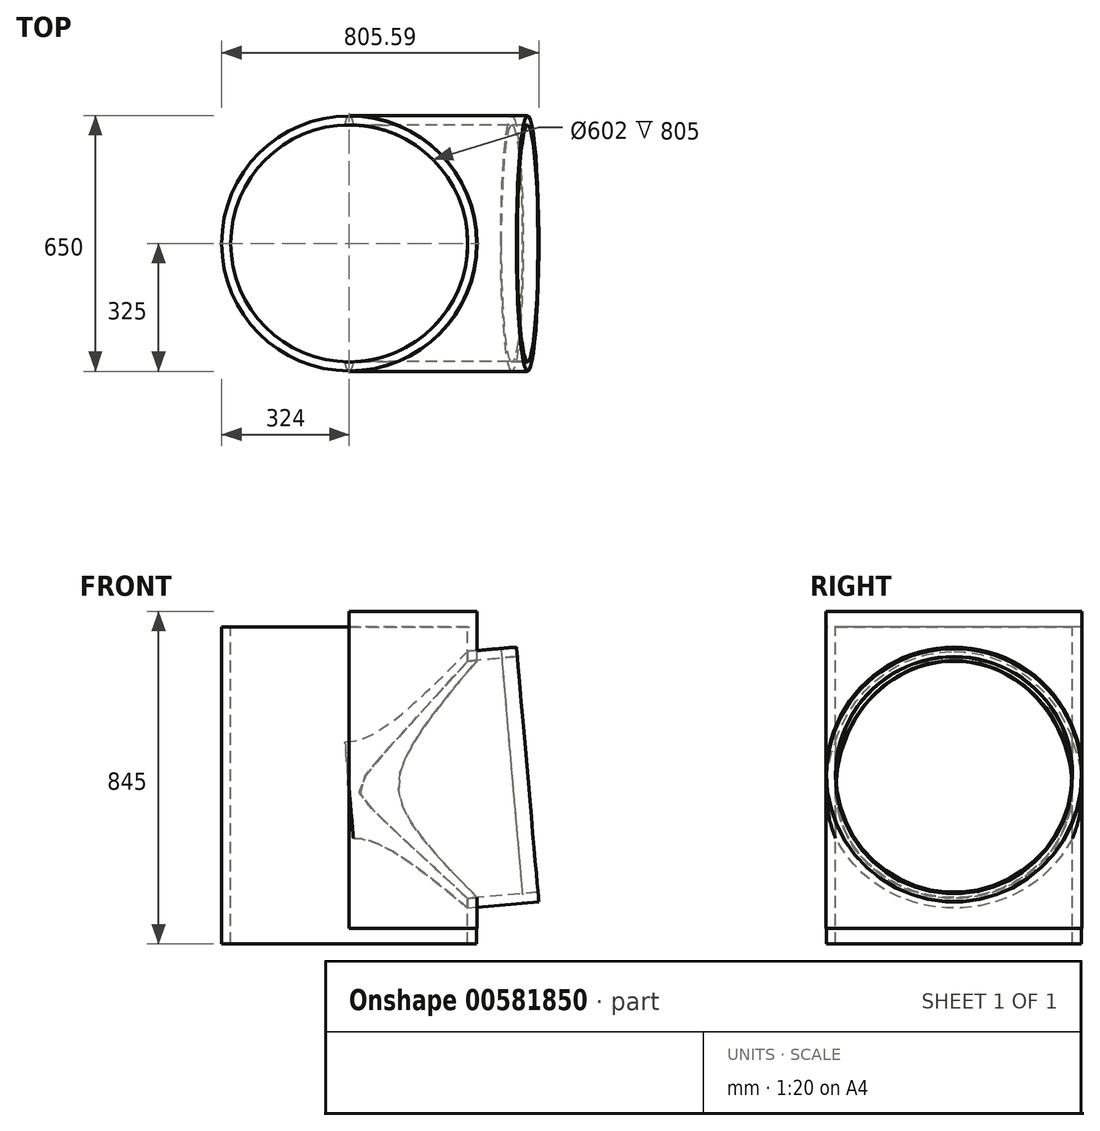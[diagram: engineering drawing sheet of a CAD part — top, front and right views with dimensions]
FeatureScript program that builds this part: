
annotation { "Feature Type Name" : "Feature", "Feature Type Description" : "" }
export const myFeature = defineFeature(function(context is Context, id is Id, definition is map)
    precondition{}
    {
        {
            var Q0;
            Q0=qCreatedBy(makeId("Front.planeOp"),FACE);
            var sketch = newSketch(context, id + "F0", { "sketchPlane" : qUnion([Q0])});
            skLineSegment(sketch, "E0", {"start": v(0, 377.94) * mm, "end": v(0, -525.84) * mm, "construction": true});
            skLineSegment(sketch, "E1", {"start": v(-325, -351) * mm, "end": v(-324, -351) * mm});
            skLineSegment(sketch, "E2", {"start": v(-324, -391) * mm, "end": v(-324, -351) * mm});
            skLineSegment(sketch, "E3", {"start": v(-324, -391) * mm, "end": v(-301, -391) * mm});
            skLineSegment(sketch, "E4", {"start": v(-301, -351) * mm, "end": v(-301, -391) * mm});
            skLineSegment(sketch, "E5", {"start": v(-301, -351) * mm, "end": v(-300, -351) * mm});
            skLineSegment(sketch, "E6", {"start": v(-576.36, 528.14) * mm, "end": v(633, -580.04) * mm, "construction": true});
            skLineSegment(sketch, "E7", {"start": v(0, 0) * mm, "end": v(-755.87, 0) * mm, "construction": true});
            skLineSegment(sketch, "E8", {"start": v(0, 0) * mm, "end": v(-73.8, 843.63) * mm, "construction": true});
            skLineSegment(sketch, "E9", {"start": v(-325, -351) * mm, "end": v(-325, 297.8) * mm});
            skLineSegment(sketch, "E10", {"start": v(-300, -351) * mm, "end": v(-300, 274.9) * mm});
            skLineSegment(sketch, "E11", {"start": v(424.94, 363.42) * mm, "end": v(425.03, 362.42) * mm});
            skLineSegment(sketch, "E12", {"start": v(385.18, 358.94) * mm, "end": v(425.03, 362.42) * mm});
            skLineSegment(sketch, "E13", {"start": v(385.18, 358.94) * mm, "end": v(387.19, 336.02) * mm});
            skLineSegment(sketch, "E14", {"start": v(427.03, 339.51) * mm, "end": v(387.19, 336.02) * mm});
            skLineSegment(sketch, "E15", {"start": v(427.03, 339.51) * mm, "end": v(427.12, 338.51) * mm});
            skLineSegment(sketch, "E16", {"start": v(427.12, 338.51) * mm, "end": v(-26.15, 298.86) * mm});
            skLineSegment(sketch, "E17", {"start": v(0, 0) * mm, "end": v(388.36, 33.98) * mm, "construction": true});
            skLineSegment(sketch, "E18", {"start": v(-300, 274.9) * mm, "end": v(-300, 454) * mm});
            skLineSegment(sketch, "E19", {"start": v(-300, 454) * mm, "end": v(-301, 454) * mm});
            skLineSegment(sketch, "E20", {"start": v(-301, 414) * mm, "end": v(-301, 454) * mm});
            skLineSegment(sketch, "E21", {"start": v(-301, 414) * mm, "end": v(-324, 414) * mm});
            skLineSegment(sketch, "E22", {"start": v(-324, 454) * mm, "end": v(-324, 414) * mm});
            skLineSegment(sketch, "E23", {"start": v(-324, 454) * mm, "end": v(-325, 454) * mm});
            skLineSegment(sketch, "E24", {"start": v(-325, 454) * mm, "end": v(-325, 297.8) * mm});
            skLineSegment(sketch, "E25.trimOffspring", {"start": v(-28.33, 323.76) * mm, "end": v(424.94, 363.42) * mm});
            skLineSegment(sketch, "E26", {"start": v(-28.33, 323.76) * mm, "end": v(-26.15, 298.86) * mm});
            skSolve(sketch);
        }
        {
            var Q0;
            Q0=makeQuery(id+"F0.imprint","IMPRINT",FACE,{"disambiguationData":[TD([[makeQuery(id+"F0.imprint","IMPRINT",EDGE,{"derivedFrom":sQuery(id+"F0.wireOp",EDGE,"E1")}),1.0]])]});
            var Q1;
            Q1=sQuery(id+"F0.wireOp",EDGE,"E0");
            revolve(context, id + "F1", {"entities" : qUnion([Q0]), "axis" : qUnion([Q1]), "revolveType" : RevolveType.FULL});
        }
        {
            var Q0;
            Q0=makeQuery(id+"F0.imprint","IMPRINT",FACE,{"disambiguationData":[TD([[makeQuery(id+"F0.imprint","IMPRINT",EDGE,{"derivedFrom":sQuery(id+"F0.wireOp",EDGE,"E11")}),-1.0]])]});
            var Q1;
            Q1=sQuery(id+"F0.wireOp",EDGE,"E17");
            revolve(context, id + "F2", {"entities" : qUnion([Q0]), "axis" : qUnion([Q1]), "revolveType" : RevolveType.FULL});
        }
        {
            var Q0;
            Q0=makeQuery(id+"F2.opRevolve","SWEPT_FACE",FACE,{"disambiguationData":[OSD([sQuery(id+"F0.wireOp",EDGE,"E13")])]});
            var sketch = newSketch(context, id + "F3", { "sketchPlane" : qUnion([Q0])});
            skCircle(sketch, "E27.0", {"center": v(0, 0) * mm, "radius": 300 * mm});
            skSolve(sketch);
        }
        {
            var Q0;
            Q0=qSketchRegion(id+"F3",true);
            var Q1;
            Q1=makeQuery(id+"F2.opRevolve","SWEPT_FACE",FACE,{"disambiguationData":[OSD([sQuery(id+"F0.wireOp",EDGE,"RudJvVgb-d4Mj-z1rT-Vhq7-xhC1Clk5OM9b")])]});
            extrude(context, id + "F4", {"entities" : qUnion([Q0]), "operationType" : NewBodyOperationType.REMOVE, "flatOperationType" : FlatOperationType.REMOVE, "oppositeDirection" : true, "depth" : 415 * mm, "endBoundEntityFace" : qUnion([Q1]), "offsetDistance" : 25 * mm, "domain" : OperationDomain.MODEL});
        }
        {
            var Q0;
            Q0=makeQuery(id+"F1.opRevolve","SWEPT_FACE",FACE,{"disambiguationData":[OSD([sQuery(id+"F0.wireOp",EDGE,"E3")])]});
            cPlane(context, id + "F5", {"entities" : qUnion([Q0]), "cplaneType" : CPlaneType.OFFSET, "offset" : 500 * mm, "width" : 150 * mm, "height" : 150 * mm});
        }
        {
            var Q0;
            Q0=qCreatedBy(id+"F5.planeOp",FACE);
            var sketch = newSketch(context, id + "F6", { "sketchPlane" : qUnion([Q0])});
            skCircle(sketch, "E28.0", {"center": v(0, 0) * mm, "radius": 301 * mm});
            skCircle(sketch, "E29.0", {"center": v(0, 0) * mm, "radius": 324 * mm, "construction": true});
            skArc(sketch, "E30", {"start": v(0, -324) * mm, "mid": v(-324, 0) * mm, "end": v(0, 324) * mm});
            skLineSegment(sketch, "E31", {"start": v(0, 324) * mm, "end": v(0, 672.32) * mm});
            skArc(sketch, "E32", {"start": v(0, 672.32) * mm, "mid": v(-672.32, 0) * mm, "end": v(0, -672.32) * mm});
            skLineSegment(sketch, "E33", {"start": v(0, -324) * mm, "end": v(0, -672.32) * mm});
            skSolve(sketch);
        }
        {
            var Q0;
            Q0=qSketchRegion(id+"F6",true);
            extrude(context, id + "F7", {"entities" : qUnion([Q0]), "operationType" : NewBodyOperationType.REMOVE, "flatOperationType" : FlatOperationType.REMOVE, "oppositeDirection" : true, "depth" : 3000 * mm, "offsetDistance" : 25 * mm, "domain" : OperationDomain.MODEL});
        }
    });
